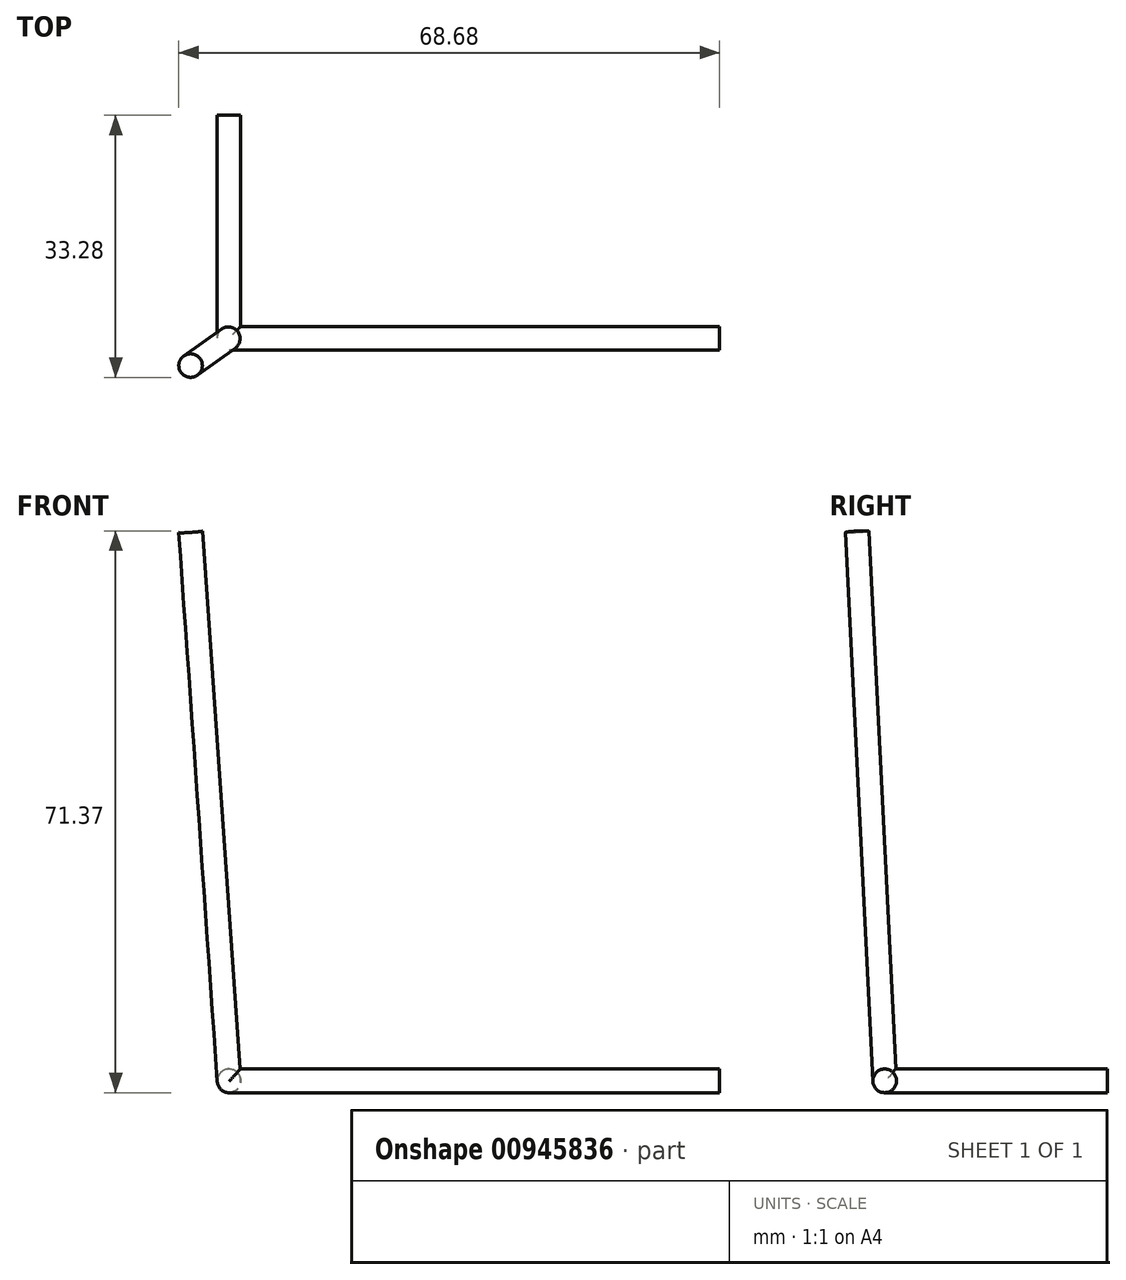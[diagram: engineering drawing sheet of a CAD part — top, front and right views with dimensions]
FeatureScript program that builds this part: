
annotation { "Feature Type Name" : "Feature", "Feature Type Description" : "" }
export const myFeature = defineFeature(function(context is Context, id is Id, definition is map)
    precondition{}
    {
        {
            var Q0;
            Q0=qCreatedBy(makeId("Right.planeOp"),FACE);
            var sketch = newSketch(context, id + "F0", { "sketchPlane" : qUnion([Q0])});
            skCircle(sketch, "E0", {"center": v(0, -40) * mm, "radius": 1.5 * mm});
            skSolve(sketch);
        }
        {
            var Q0;
            Q0 = qSketchRegion(id + "F0", true);
            extrude(context, id + "F1", {"entities" : qUnion([Q0]), "depth" : (64 - 1.7) * mm, "offsetDistance" : 25 * mm});
        }
        {
            var Q0;
            Q0=qCreatedBy(makeId("Front.planeOp"),FACE);
            var sketch = newSketch(context, id + "F2", { "sketchPlane" : qUnion([Q0])});
            skCircle(sketch, "E1", {"center": v(0, -40) * mm, "radius": 1.5 * mm});
            skSolve(sketch);
        }
        {
            var Q0;
            Q0 = qSketchRegion(id + "F2", true);
            extrude(context, id + "F3", {"entities" : qUnion([Q0]), "operationType" : NewBodyOperationType.ADD, "oppositeDirection" : true, "depth" : (30 - 1.7) * mm, "offsetDistance" : 25 * mm});
        }
        {
            var Q0;
            Q0=makeQuery(id+"F1.opExtrude","CAP_FACE",FACE,{"disambiguationData":[OSD([sQuery(id+"F0.wireOp",EDGE,"E0")])],"isStart":true});
            var sketch = newSketch(context, id + "F4", { "sketchPlane" : qUnion([Q0])});
            skArc(sketch, "E2", {"start": v(0, -41.5) * mm, "mid": v(1.5, -40) * mm, "end": v(0, -38.5) * mm});
            skLineSegment(sketch, "E3", {"start": v(0, -38.5) * mm, "end": v(0, -41.5) * mm});
            skSolve(sketch);
        }
        {
            var Q0;
            Q0 = qSketchRegion(id + "F4", true);
            var Q1;
            Q1=sQuery(id+"F4.wireOp",EDGE,"E3");
            revolve(context, id + "F5", {"operationType" : NewBodyOperationType.ADD, "surfaceOperationType" : NewSurfaceOperationType.NEW, "entities" : qUnion([Q0]), "axis" : qUnion([Q1]), "revolveType" : RevolveType.ONE_DIRECTION, "angle" : 90 * degree});
        }
        {
            var Q0;
            Q0=qCreatedBy(makeId("Top.planeOp"),FACE);
            cPlane(context, id + "F6", {"entities" : qUnion([Q0]), "cplaneType" : CPlaneType.OFFSET, "offset" : 40 * mm, "oppositeDirection" : true, "width" : 150 * mm, "height" : 150 * mm});
        }
        {
            var Q0;
            Q0=qCreatedBy(makeId("Front.planeOp"),FACE);
            var sketch = newSketch(context, id + "F7", { "sketchPlane" : qUnion([Q0])});
            skLineSegment(sketch, "E4", {"start": v(-4.72, -40) * mm, "end": v(19.82, -40) * mm, "construction": true});
            skSolve(sketch);
        }
        {
            var Q0;
            Q0=qCreatedBy(id+"F6.planeOp",FACE);
            var Q1;
            Q1=sQuery(id+"F7.wireOp",EDGE,"E4");
            cPlane(context, id + "F8", {"entities" : qUnion([Q0, Q1]), "cplaneType" : CPlaneType.LINE_ANGLE, "offset" : 25 * mm, "angle" : 92.86 * degree, "width" : 150 * mm, "height" : 150 * mm});
        }
        {
            var Q0;
            Q0=qCreatedBy(id+"F8.planeOp",FACE);
            var Q1;
            Q1=sQuery(id+"F7.wireOp",EDGE,"E4");
            cPlane(context, id + "F9", {"entities" : qUnion([Q0, Q1]), "cplaneType" : CPlaneType.LINE_ANGLE, "offset" : 25 * mm, "angle" : 90 * degree, "width" : 150 * mm, "height" : 150 * mm});
        }
        {
            var Q0;
            Q0=qCreatedBy(makeId("Right.planeOp"),FACE);
            var sketch = newSketch(context, id + "F10", { "sketchPlane" : qUnion([Q0])});
            skLineSegment(sketch, "E5", {"start": v(4.08, -39.8) * mm, "end": v(-4.89, -40.24) * mm, "construction": true});
            skSolve(sketch);
        }
        {
            var Q0;
            Q0=qCreatedBy(id+"F9.planeOp",FACE);
            var Q1;
            Q1=sQuery(id+"F10.wireOp",EDGE,"E5");
            cPlane(context, id + "F11", {"entities" : qUnion([Q0, Q1]), "cplaneType" : CPlaneType.LINE_ANGLE, "offset" : 25 * mm, "angle" : 4 * degree, "width" : 150 * mm, "height" : 150 * mm});
        }
        {
            var Q0;
            Q0=qCreatedBy(id+"F11.planeOp",FACE);
            var sketch = newSketch(context, id + "F12", { "sketchPlane" : qUnion([Q0])});
            skCircle(sketch, "E6", {"center": v(-2.79, -2) * mm, "radius": 1.5 * mm});
            skSolve(sketch);
        }
        {
            var Q0;
            Q0 = qSketchRegion(id + "F12", true);
            extrude(context, id + "F13", {"entities" : qUnion([Q0]), "operationType" : NewBodyOperationType.ADD, "depth" : 70 * mm, "offsetDistance" : 25 * mm});
        }
    });
